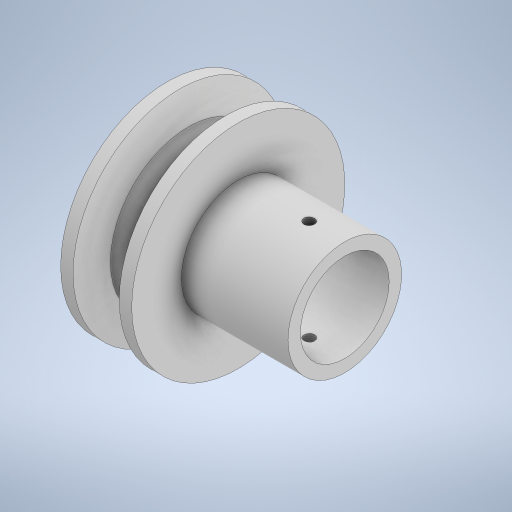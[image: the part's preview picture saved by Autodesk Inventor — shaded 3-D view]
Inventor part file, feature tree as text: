
AUTODESK INVENTOR PART (.ipt)
format: ipt  version: 2023 (Build 270158000, 158)  size: 307,712 bytes
history: native  units: mm
features: sketch x2, revolve x1, extrude x1, thread x1
ambient origin geometry x8: Origin, YZ Plane, XZ Plane, XY Plane, X Axis, Y Axis, Z Axis, Center Point
bodies: Body1 (feature_tree)
feature tree (5):
  sketch  "Эскиз1"
  revolve  "Вращение3"
  extrude  "Выдавливание3"  Depth=30.0mm
  thread  "Резьба2"
  sketch  "Эскиз3"
